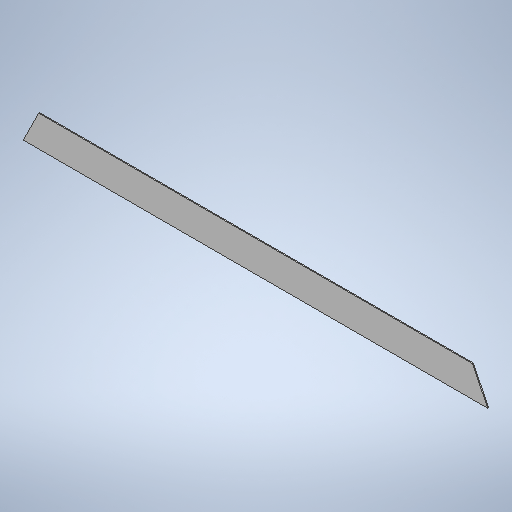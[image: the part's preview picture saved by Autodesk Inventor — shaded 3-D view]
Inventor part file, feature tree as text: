
AUTODESK INVENTOR PART (.ipt)
format: ipt  version: 2025 (Build 290162010, 162A)  size: 272,896 bytes
history: native  units: mm
features: other x3, sheet_metal_op x1, sketch x1
ambient origin geometry x8: Origin, YZ Plane, XZ Plane, XY Plane, X Axis, Y Axis, Z Axis, Center Point
bodies: Solid1 (feature_tree)
feature tree (5):
  other  "MSC 204 GRID"
  sheet_metal_op  "Face1"
  sketch  "Sketch1"  dims[d0=100.0mm d1=1800.0mm d2=3.0mm d3=20.333086mm d6=698.5mm d7=20.333086mm d8=698.5mm]
  other  "Plate1"
  other  "Definition1"
